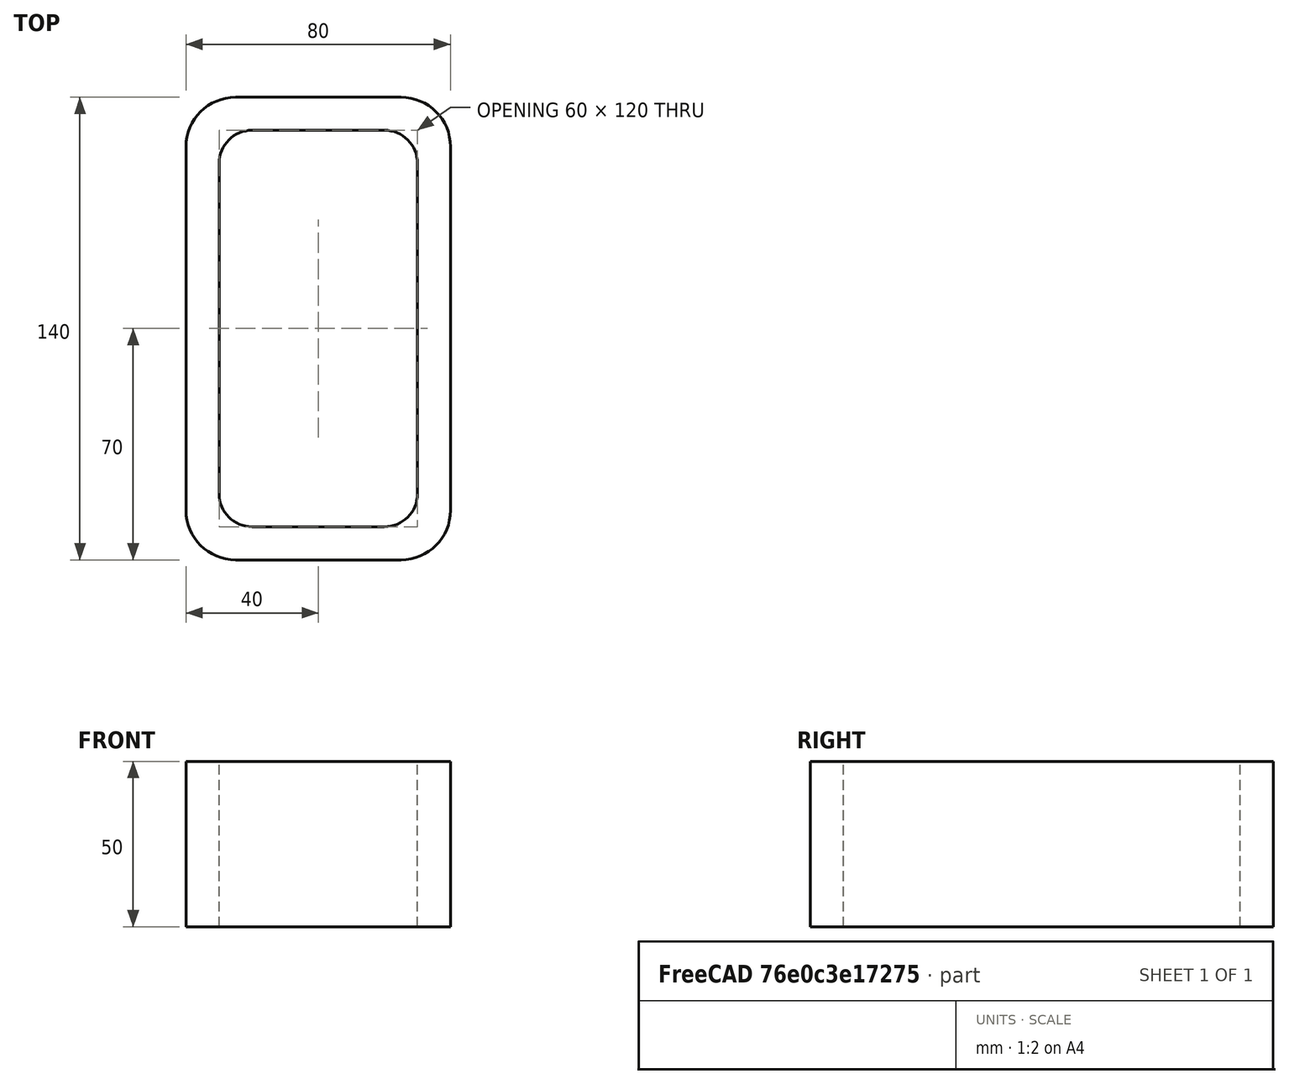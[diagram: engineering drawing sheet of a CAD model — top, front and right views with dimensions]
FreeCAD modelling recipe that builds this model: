
FCSTD DOCUMENT  (FreeCAD 0.15R4671 (Git))
Label: Rectangular hollow section 140x80x10 EN10219 S235JRH
License: All rights reserved
LicenseURL: http://en.wikipedia.org/wiki/All_rights_reserved
objects: Sketcher::SketchObject×1, Part::Extrusion×1
note: 2 computed .brp shape members not serialized (recipe doc carries the construction recipe); baked Part::Feature solids carry a one-line shape summary decoded from their .brp

FEATURE [Sketcher::SketchObject] Sketch
  sketch-geometry (16):
    g0: LineSegment StartX=-20 StartY=60 StartZ=0 EndX=20 EndY=60 EndZ=0
    g1: LineSegment StartX=30 StartY=50 StartZ=0 EndX=30 EndY=-50 EndZ=0
    g2: LineSegment StartX=20 StartY=-60 StartZ=0 EndX=-20 EndY=-60 EndZ=0
    g3: LineSegment StartX=-30 StartY=-50 StartZ=0 EndX=-30 EndY=50 EndZ=0
    g4: LineSegment StartX=-25 StartY=70 StartZ=0 EndX=25 EndY=70 EndZ=0
    g5: LineSegment StartX=40 StartY=55 StartZ=0 EndX=40 EndY=-55 EndZ=0
    g6: LineSegment StartX=25 StartY=-70 StartZ=0 EndX=-25 EndY=-70 EndZ=0
    g7: LineSegment StartX=-40 StartY=-55 StartZ=0 EndX=-40 EndY=55 EndZ=0
    g8: ArcOfCircle CenterX=-20 CenterY=50 CenterZ=0 NormalX=0 NormalY=0 NormalZ=1 Radius=10 StartAngle=1.5708 EndAngle=3.14159
    g9: ArcOfCircle CenterX=20 CenterY=50 CenterZ=0 NormalX=0 NormalY=0 NormalZ=1 Radius=10 StartAngle=0 EndAngle=1.5708
    g10: ArcOfCircle CenterX=20 CenterY=-50 CenterZ=0 NormalX=0 NormalY=0 NormalZ=1 Radius=10 StartAngle=4.71239 EndAngle=6.28319
    g11: ArcOfCircle CenterX=-20 CenterY=-50 CenterZ=0 NormalX=0 NormalY=0 NormalZ=1 Radius=10 StartAngle=3.14159 EndAngle=4.71239
    g12: ArcOfCircle CenterX=25 CenterY=55 CenterZ=0 NormalX=0 NormalY=0 NormalZ=1 Radius=15 StartAngle=0 EndAngle=1.5708
    g13: ArcOfCircle CenterX=25 CenterY=-55 CenterZ=0 NormalX=0 NormalY=0 NormalZ=1 Radius=15 StartAngle=4.71239 EndAngle=6.28319
    g14: ArcOfCircle CenterX=-25 CenterY=-55 CenterZ=0 NormalX=0 NormalY=0 NormalZ=1 Radius=15 StartAngle=3.14159 EndAngle=4.71239
    g15: ArcOfCircle CenterX=-25 CenterY=55 CenterZ=0 NormalX=0 NormalY=0 NormalZ=1 Radius=15 StartAngle=1.5708 EndAngle=3.14159
  constraints (36):
    c: Horizontal(g2)
    c: Vertical(g3)
    c: Horizontal(g6)
    c: Vertical(g7)
    c: Tangent(g3,g8) = 1.5708
    c: Tangent(g0,g8) = 1.5708
    c: Tangent(g0,g9) = 1.5708
    c: Tangent(g1,g9) = 1.5708
    c: Tangent(g1,g10) = 1.5708
    c: Tangent(g2,g10) = 1.5708
    c: Tangent(g2,g11) = 1.5708
    c: Tangent(g3,g11) = 1.5708
    c: Tangent(g4,g12) = 1.5708
    c: Tangent(g5,g12) = 1.5708
    c: Tangent(g5,g13) = 1.5708
    c: Tangent(g6,g13) = 1.5708
    c: Tangent(g6,g14) = 1.5708
    c: Tangent(g7,g14) = 1.5708
    c: Tangent(g7,g15) = 1.5708
    c: Tangent(g4,g15) = 1.5708
    c: Equal(g9,g8)
    c: Equal(g9,g11)
    c: Equal(g9,g10)
    c: Equal(g12,g15)
    c: Equal(g12,g14)
    c: Equal(g12,g13)
    c: Symmetric(g4,g6,g-1)
    c: Symmetric(g7,g5,g-2)
    c: DistanceY(g4,g6) = -140
    c: DistanceX(g7,g5) = 80
    c: Symmetric(g3,g1,g-2)
    c: Symmetric(g0,g2,g-1)
    c: DistanceY(g0,g4) = 10
    c: DistanceX(g5,g1) = -10
    c: Radius(g9) = 10
    c: Radius(g12) = 15
FEATURE [Part::Extrusion] Extrude  label="Rectangular hollow section 140x80x10 EN10219 S235JRH"
  Base = -> Sketch
  Dir = (0,0,50)
  Solid = true
